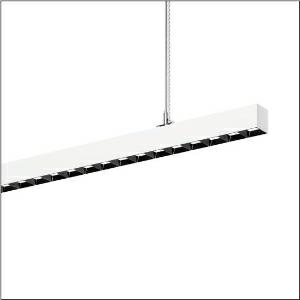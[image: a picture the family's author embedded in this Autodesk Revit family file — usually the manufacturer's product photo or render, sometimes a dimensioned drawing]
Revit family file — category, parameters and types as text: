
# Revit family: silica_21_51mx34dc3dwb
name_source: partatom
category: Lighting Fixtures
units: mm (PartAtom-declared; Revit-internal decimal feet)

## family parameters
Cut with Voids When Loaded = No
Host = Face
Light Source = No
Part Type = Normal
Room Calculation Point = No
Round Connector Dimension = Use Diameter
Shared = No

## types (1)
- --- (1 x LED, 19200 lm, 129.1 W, 3000K)
    Apparent Load = 129 VA
    CIE Flux Codes = 74 94 99 56 100
    Color Rendering = 80
    Color Temperature = 3000K
    Default Elevation = 1800 mm
    Description = Silica 21, office luminaire, primary light control with darklight reflector, of PMMA, black, light emission: direct/indirect distribution, primary light characteristic: asymmetric, installation type: suspended mounting, LED, rated luminous flux: 19.200lm, luminous efficacy: 149lm/W, light colour: 830, colour temperature: 3000K, control gear: DALI 2, with terminal, 3+2-pole, max. 2.5mm², mains connection: 220..240V, AC, 50/60Hz, rated input power: 129.1W, luminaire housing, of aluminium, traffic white (RAL 9016), length: 3.004mm, width: 53mm, height: 53mm, protection rating (complete): IP20, insulation class (complete): insulation class I (protective earthing), certification: CE, permissible operating ambient temperature: 0..+35°C, standard: EN 50419, packaging unit: 1 piece
    Height = 53 mm
    Lamp = 1 x LED
    Lamp Light Flux = 19200 lm
    Lamp Power = 129.1 W
    Lamp count = 1
    Length = 3004 mm
    Luminous efficacy = 149 lm/W
    Manufacturer = Siteco
    ModVariant = No
    Model = 51MX34DC3DWB
    Mounting Place = Ceiling
    Mounting Type = Pendant
    Number of Poles = 1
    OnlyDefault = Yes
    Power Factor = 1
    Product Name = Silica 21
    Product group = office luminaire | ceiling pendant
    ProductGroupID = 903
    Protection Class = Protection class I
    Protection Degree = IP 20
    RLX_Detail_Level = 1
    RLX_Emergency_Light_Flux = 0 lm
    RLX_Emergency_Type = 0
    RLX_Emergency_Type_DB = No
    RlxData = <blob elided: 65961 chars, md5=4ae59d87>
    Socket = socket
    Standby Power = 0 W
    System Light Flux = 19200 lm
    System Power = 129 W
    Type Comments = factory setting: luminous flux: 100 % | dim-lin: 254 | 448 mA
    Type Image = l_1335871.jpg
    URL = http://relux.com
    VarID = @adj_120429
    Voltage = 0 V
    Weight = 0.00 kg
    Width = 53 mm

## geometry (parser evidence)
native form markers: Blend x4, Sweep x11
no freeform markers — native parametric forms only
